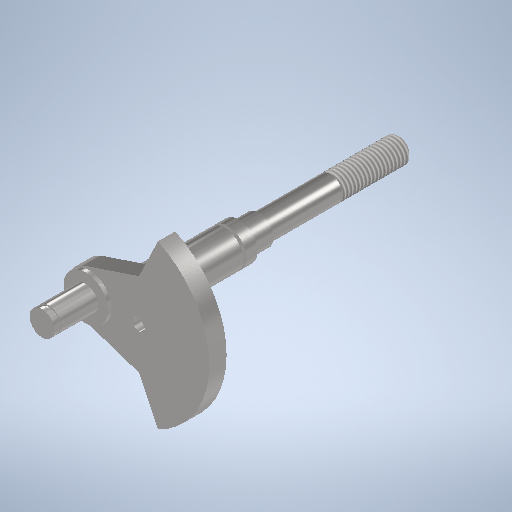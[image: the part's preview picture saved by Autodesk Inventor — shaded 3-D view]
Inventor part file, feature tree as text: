
AUTODESK INVENTOR PART (.ipt)
format: ipt  version: 2025 (Build 290162010, 162A)  size: 372,736 bytes
history: native  units: mm
features: sketch x4, extrude x2, plane x2, revolve x2, thread x1, chamfer x1, projected_geometry x1
ambient origin geometry x8: Origin, YZ Plane, XZ Plane, XY Plane, X Axis, Y Axis, Z Axis, Center Point
bodies: Volumenkörper1 (feature_tree)
feature tree (13):
  extrude  "Extrusion1"  Depth=36.5mm
  plane  "Arbeitsebene1"
  revolve  "Umdrehung2"
  revolve  "Umdrehung1"
  thread  "Gewinde1"  [1 undecoded]
  chamfer  "Fasen1"  Distance=7.0mm
  plane  "Work Plane3"
  extrude  "Extrusion2"  Depth=10.0mm
  sketch  "Skizze1"  dims[d0=6.457718mm d2=22.514747mm d3=36.5mm]
  sketch  "Skizze3"  dims[d5=10.0mm d6=7.0mm d7=0.0mm]
  sketch  "Skizze5"  dims[d10=0.0mm d13=10.0mm]
  projected_geometry  "Projected Loop1"
  sketch  "Sketch8"  dims[d14=12.0mm d15=15.0mm d16=17.0mm d18=22.0mm d20=1.5mm d21=1.2mm d22=4.5mm d25=90.0deg d26=28.0mm d27=0.0mm d28=1.0mm d29=2.0mm d30=45.0deg d32=9.0mm d33=1.5mm d35=1.1mm d36=15.0mm d37=10.0mm d38=9.0mm d39=18.0mm d40=90.0deg d41=2.7mm d44=13.0mm d45=8.0mm d46=57.0mm d47=28.0mm d48=106.0mm d49=8.5mm d53=11.0mm d54=5.0mm d55=3.0mm d56=0.0mm]
note: 1 required parameter value undecoded (feature->parameter linkage not recoverable at this tier; creation-order binding heuristic only, values carry confidence <= 0.55)
